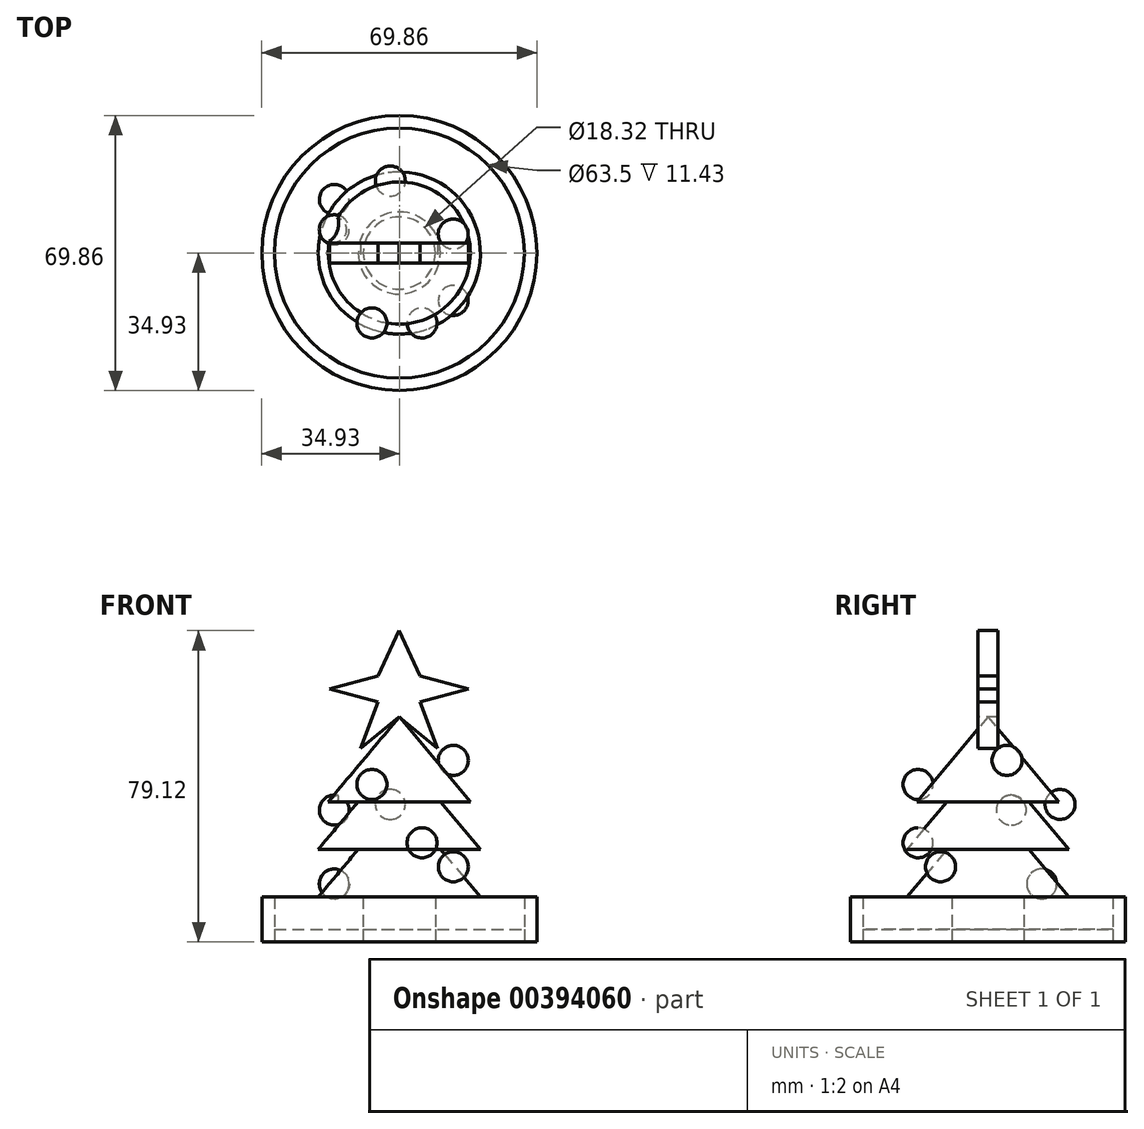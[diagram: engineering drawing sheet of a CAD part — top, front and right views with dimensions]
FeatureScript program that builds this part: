
annotation { "Feature Type Name" : "Feature", "Feature Type Description" : "" }
export const myFeature = defineFeature(function(context is Context, id is Id, definition is map)
    precondition{}
    {
        {
            var Q0;
            Q0=qCreatedBy(makeId("Front.planeOp"),FACE);
            var sketch = newSketch(context, id + "F0", { "sketchPlane" : qUnion([Q0])});
            skLineSegment(sketch, "E0", {"start": v(0, -31.26) * mm, "end": v(0, 38.6) * mm});
            skLineSegment(sketch, "E1", {"start": v(9.16, -18.56) * mm, "end": v(9.16, -7.13) * mm});
            skLineSegment(sketch, "E2", {"start": v(9.16, -7.13) * mm, "end": v(0, -7.13) * mm});
            skLineSegment(sketch, "E3.left", {"start": v(0, -31.26) * mm, "end": v(0, -18.56) * mm});
            skLineSegment(sketch, "E4", {"start": v(9.16, -7.13) * mm, "end": v(20.59, -7.13) * mm});
            skLineSegment(sketch, "E5", {"start": v(20.59, -7.13) * mm, "end": v(10.43, 4.98) * mm});
            skLineSegment(sketch, "E6", {"start": v(10.43, 4.98) * mm, "end": v(20.59, 4.98) * mm});
            skLineSegment(sketch, "E7", {"start": v(20.59, 4.98) * mm, "end": v(10.43, 17.08) * mm});
            skLineSegment(sketch, "E8", {"start": v(10.43, 17.08) * mm, "end": v(18.05, 17.08) * mm});
            skLineSegment(sketch, "E9", {"start": v(0, 38.6) * mm, "end": v(18.05, 17.08) * mm});
            skLineSegment(sketch, "E10", {"start": v(9.16, -18.56) * mm, "end": v(0, -18.56) * mm});
            skSolve(sketch);
        }
        {
            var Q0;
            {var subQ0=sQuery(id+"F0.wireOp",EDGE,"E2");Q0=makeQuery(id+"F0.imprint","IMPRINT",FACE,{"disambiguationData":[TD([[makeQuery(id+"F0.imprint","IMPRINT",EDGE,{"derivedFrom":subQ0}),-1.0]])]});}
            var Q1;
            Q1=sQuery(id+"F0.wireOp",EDGE,"E0");
            revolve(context, id + "F1", {"entities" : qUnion([Q0]), "axis" : qUnion([Q1]), "revolveType" : RevolveType.FULL});
        }
        {
            var Q0;
            {var subQ4=sQuery(id+"F0.wireOp",EDGE,"E1");Q0=makeQuery(id+"F0.imprint","IMPRINT",FACE,{"disambiguationData":[TD([[makeQuery(id+"F0.imprint","IMPRINT",EDGE,{"derivedFrom":subQ4}),1.0]])]});}
            var Q1;
            Q1=sQuery(id+"F0.wireOp",EDGE,"E0");
            revolve(context, id + "F2", {"entities" : qUnion([Q0]), "axis" : qUnion([Q1]), "revolveType" : RevolveType.FULL});
        }
        {
            var Q0;
            Q0=makeQuery(id+"F2.opRevolve","SWEPT_FACE",FACE,{"disambiguationData":[OSD([sQuery(id+"F0.wireOp",EDGE,"E10")])]});
            var sketch = newSketch(context, id + "F3", { "sketchPlane" : qUnion([Q0])});
            skCircle(sketch, "E11", {"center": v(0, 0) * mm, "radius": 31.75 * mm});
            skCircle(sketch, "E12", {"center": v(0, 0) * mm, "radius": 34.93 * mm});
            skSolve(sketch);
        }
        {
            var Q0;
            Q0=makeQuery(id+"F3.imprint","IMPRINT",FACE,{"disambiguationData":[TD([[makeQuery(id+"F3.imprint","IMPRINT",EDGE,{"derivedFrom":sQuery(id+"F3.wireOp",EDGE,"E11")}),-1.0]])]});
            extrude(context, id + "F4", {"entities" : qUnion([Q0]), "oppositeDirection" : true, "depth" : 11.43 * mm});
        }
        {
            var Q0;
            Q0=makeQuery(id+"F3.imprint","IMPRINT",FACE,{"disambiguationData":[TD([[makeQuery(id+"F3.imprint","IMPRINT",EDGE,{"derivedFrom":sQuery(id+"F3.wireOp",EDGE,"E11")}),1.0]])]});
            extrude(context, id + "F5", {"entities" : qUnion([Q0]), "oppositeDirection" : true, "depth" : 3.17 * mm});
        }
        {
            var Q0;
            Q0=qCreatedBy(makeId("Front.planeOp"),FACE);
            var sketch = newSketch(context, id + "F6", { "sketchPlane" : qUnion([Q0])});
            skLineSegment(sketch, "E13", {"start": v(-0.05, 60.56) * mm, "end": v(-5.41, 49.05) * mm});
            skLineSegment(sketch, "E14", {"start": v(-5.41, 49.05) * mm, "end": v(-17.68, 45.76) * mm});
            skLineSegment(sketch, "E15", {"start": v(-17.68, 45.76) * mm, "end": v(-5.41, 42.47) * mm});
            skLineSegment(sketch, "E16", {"start": v(-5.41, 42.47) * mm, "end": v(-9.81, 30.56) * mm});
            skLineSegment(sketch, "E17", {"start": v(-9.81, 30.56) * mm, "end": v(-0.05, 38.68) * mm});
            skLineSegment(sketch, "E18.MirrorCS", {"start": v(-0.05, 60.56) * mm, "end": v(5.32, 49.05) * mm});
            skLineSegment(sketch, "E19.MirrorCS", {"start": v(5.32, 49.05) * mm, "end": v(17.59, 45.76) * mm});
            skLineSegment(sketch, "E20.MirrorCS", {"start": v(17.59, 45.76) * mm, "end": v(5.32, 42.47) * mm});
            skLineSegment(sketch, "E21.MirrorCS", {"start": v(5.32, 42.47) * mm, "end": v(9.72, 30.56) * mm});
            skLineSegment(sketch, "E22.MirrorCS", {"start": v(9.72, 30.56) * mm, "end": v(-0.05, 38.68) * mm});
            skSolve(sketch);
        }
        {
            var Q0;
            Q0=makeQuery(id+"F6.imprint","IMPRINT",FACE,{"disambiguationData":[TD([[makeQuery(id+"F6.imprint","IMPRINT",EDGE,{"derivedFrom":sQuery(id+"F6.wireOp",EDGE,"E13")}),1.0]])]});
            extrude(context, id + "F7", {"entities" : qUnion([Q0]), "oppositeDirection" : true, "depth" : 2.54 * mm, "hasSecondDirection" : true, "secondDirectionOppositeDirection" : false, "secondDirectionDepth" : 2.54 * mm});
        }
        {
            var Q0;
            Q0=qCreatedBy(makeId("Front.planeOp"),FACE);
            cPlane(context, id + "F8", {"entities" : qUnion([Q0]), "cplaneType" : CPlaneType.OFFSET, "offset" : 17.78 * mm, "width" : 152.4 * mm, "height" : 152.4 * mm});
        }
        {
            var Q0;
            Q0=qCreatedBy(id+"F8.planeOp",FACE);
            var sketch = newSketch(context, id + "F9", { "sketchPlane" : qUnion([Q0])});
            skArc(sketch, "E23", {"start": v(5.77, 10.45) * mm, "mid": v(1.96, 6.64) * mm, "end": v(5.77, 2.83) * mm});
            skPoint(sketch, "E24", {"position": v(5.77, 10.45) * mm});
            skPoint(sketch, "E25", {"position": v(5.77, 2.83) * mm});
            skLineSegment(sketch, "E26", {"start": v(5.77, 10.45) * mm, "end": v(5.77, 2.83) * mm});
            skArc(sketch, "E27", {"start": v(-6.96, 25.27) * mm, "mid": v(-10.77, 21.46) * mm, "end": v(-6.96, 17.65) * mm});
            skPoint(sketch, "E28", {"position": v(-6.96, 25.27) * mm});
            skPoint(sketch, "E29", {"position": v(-6.96, 17.65) * mm});
            skLineSegment(sketch, "E30", {"start": v(-6.96, 25.27) * mm, "end": v(-6.96, 17.65) * mm});
            skSolve(sketch);
        }
        {
            var Q0;
            Q0=makeQuery(id+"F9.imprint","IMPRINT",FACE,{"disambiguationData":[TD([[makeQuery(id+"F9.imprint","IMPRINT",EDGE,{"derivedFrom":sQuery(id+"F9.wireOp",EDGE,"E27")}),1.0]])]});
            var Q1;
            Q1=sQuery(id+"F9.wireOp",EDGE,"E30");
            revolve(context, id + "F10", {"entities" : qUnion([Q0]), "axis" : qUnion([Q1]), "revolveType" : RevolveType.FULL});
        }
        {
            var Q0;
            Q0=makeQuery(id+"F9.imprint","IMPRINT",FACE,{"disambiguationData":[TD([[makeQuery(id+"F9.imprint","IMPRINT",EDGE,{"derivedFrom":sQuery(id+"F9.wireOp",EDGE,"E23")}),1.0]])]});
            var Q1;
            Q1=sQuery(id+"F9.wireOp",EDGE,"E26");
            revolve(context, id + "F11", {"entities" : qUnion([Q0]), "axis" : qUnion([Q1]), "revolveType" : RevolveType.FULL});
        }
        {
            var Q0;
            Q0=qCreatedBy(makeId("Right.planeOp"),FACE);
            cPlane(context, id + "F12", {"entities" : qUnion([Q0]), "cplaneType" : CPlaneType.OFFSET, "offset" : 13.72 * mm, "width" : 152.4 * mm, "height" : 152.4 * mm});
        }
        {
            var Q0;
            Q0=qCreatedBy(id+"F12.planeOp",FACE);
            var sketch = newSketch(context, id + "F13", { "sketchPlane" : qUnion([Q0])});
            skArc(sketch, "E31", {"start": v(4.81, 31.4) * mm, "mid": v(1, 27.58) * mm, "end": v(4.81, 23.77) * mm});
            skPoint(sketch, "E32", {"position": v(4.81, 31.4) * mm});
            skPoint(sketch, "E33", {"position": v(4.81, 23.77) * mm});
            skLineSegment(sketch, "E34", {"start": v(4.81, 31.4) * mm, "end": v(4.81, 23.77) * mm});
            skArc(sketch, "E35", {"start": v(-12.06, 4.35) * mm, "mid": v(-15.87, 0.54) * mm, "end": v(-12.06, -3.27) * mm});
            skPoint(sketch, "E36", {"position": v(-12.06, 4.35) * mm});
            skPoint(sketch, "E37", {"position": v(-12.06, -3.27) * mm});
            skLineSegment(sketch, "E38", {"start": v(-12.06, 4.35) * mm, "end": v(-12.06, -3.27) * mm});
            skSolve(sketch);
        }
        {
            var Q0;
            Q0=makeQuery(id+"F13.imprint","IMPRINT",FACE,{"disambiguationData":[TD([[makeQuery(id+"F13.imprint","IMPRINT",EDGE,{"derivedFrom":sQuery(id+"F13.wireOp",EDGE,"E31")}),1.0]])]});
            var Q1;
            Q1=sQuery(id+"F13.wireOp",EDGE,"E34");
            revolve(context, id + "F14", {"entities" : qUnion([Q0]), "axis" : qUnion([Q1]), "revolveType" : RevolveType.FULL});
        }
        {
            var Q0;
            Q0=makeQuery(id+"F13.imprint","IMPRINT",FACE,{"disambiguationData":[TD([[makeQuery(id+"F13.imprint","IMPRINT",EDGE,{"derivedFrom":sQuery(id+"F13.wireOp",EDGE,"E35")}),1.0]])]});
            var Q1;
            Q1=sQuery(id+"F13.wireOp",EDGE,"E38");
            revolve(context, id + "F15", {"entities" : qUnion([Q0]), "axis" : qUnion([Q1]), "revolveType" : RevolveType.FULL});
        }
        {
            var Q0;
            Q0=qCreatedBy(makeId("Front.planeOp"),FACE);
            cPlane(context, id + "F16", {"entities" : qUnion([Q0]), "cplaneType" : CPlaneType.OFFSET, "offset" : 18.29 * mm, "oppositeDirection" : true, "width" : 152.4 * mm, "height" : 152.4 * mm});
        }
        {
            var Q0;
            Q0=qCreatedBy(id+"F16.planeOp",FACE);
            var sketch = newSketch(context, id + "F17", { "sketchPlane" : qUnion([Q0])});
            skArc(sketch, "E39", {"start": v(-2.29, 20.2) * mm, "mid": v(-6.1, 16.39) * mm, "end": v(-2.29, 12.58) * mm});
            skPoint(sketch, "E40", {"position": v(-2.29, 20.2) * mm});
            skPoint(sketch, "E41", {"position": v(-2.29, 12.58) * mm});
            skLineSegment(sketch, "E42", {"start": v(-2.29, 20.2) * mm, "end": v(-2.29, 12.58) * mm});
            skSolve(sketch);
        }
        {
            var Q0;
            Q0=makeQuery(id+"F17.imprint","IMPRINT",FACE,{"disambiguationData":[TD([[makeQuery(id+"F17.imprint","IMPRINT",EDGE,{"derivedFrom":sQuery(id+"F17.wireOp",EDGE,"E39")}),1.0]])]});
            var Q1;
            Q1=sQuery(id+"F17.wireOp",EDGE,"E42");
            revolve(context, id + "F18", {"entities" : qUnion([Q0]), "axis" : qUnion([Q1]), "revolveType" : RevolveType.FULL});
        }
        {
            var Q0;
            Q0=qCreatedBy(makeId("Right.planeOp"),FACE);
            cPlane(context, id + "F19", {"entities" : qUnion([Q0]), "cplaneType" : CPlaneType.OFFSET, "offset" : 16.5 * mm, "oppositeDirection" : true, "width" : 152.4 * mm, "height" : 152.4 * mm});
        }
        {
            var Q0;
            Q0=qCreatedBy(id+"F19.planeOp",FACE);
            var sketch = newSketch(context, id + "F20", { "sketchPlane" : qUnion([Q0])});
            skArc(sketch, "E43", {"start": v(5.9, 18.75) * mm, "mid": v(2.1, 14.94) * mm, "end": v(5.9, 11.13) * mm});
            skPoint(sketch, "E44", {"position": v(5.9, 18.75) * mm});
            skPoint(sketch, "E45", {"position": v(5.9, 11.13) * mm});
            skLineSegment(sketch, "E46", {"start": v(5.9, 18.75) * mm, "end": v(5.9, 11.13) * mm});
            skArc(sketch, "E47", {"start": v(13.64, 0) * mm, "mid": v(9.81, -3.8) * mm, "end": v(13.62, -7.62) * mm});
            skPoint(sketch, "E48", {"position": v(13.64, 0) * mm});
            skPoint(sketch, "E49", {"position": v(13.62, -7.62) * mm});
            skLineSegment(sketch, "E50", {"start": v(13.64, 0) * mm, "end": v(13.62, -7.62) * mm});
            skSolve(sketch);
        }
        {
            var Q0;
            Q0=makeQuery(id+"F20.imprint","IMPRINT",FACE,{"disambiguationData":[TD([[makeQuery(id+"F20.imprint","IMPRINT",EDGE,{"derivedFrom":sQuery(id+"F20.wireOp",EDGE,"E43")}),1.0]])]});
            var Q1;
            Q1=sQuery(id+"F20.wireOp",EDGE,"E46");
            revolve(context, id + "F21", {"operationType" : NewBodyOperationType.ADD, "entities" : qUnion([Q0]), "axis" : qUnion([Q1]), "revolveType" : RevolveType.FULL});
        }
        {
            var Q0;
            Q0=makeQuery(id+"F20.imprint","IMPRINT",FACE,{"disambiguationData":[TD([[makeQuery(id+"F20.imprint","IMPRINT",EDGE,{"derivedFrom":sQuery(id+"F20.wireOp",EDGE,"E47")}),1.0]])]});
            var Q1;
            Q1=sQuery(id+"F20.wireOp",EDGE,"E50");
            revolve(context, id + "F22", {"entities" : qUnion([Q0]), "axis" : qUnion([Q1]), "revolveType" : RevolveType.FULL});
        }
    });
